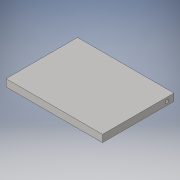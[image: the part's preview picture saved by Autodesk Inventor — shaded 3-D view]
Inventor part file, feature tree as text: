
AUTODESK INVENTOR PART (.ipt)
format: ipt  version: 2016 (Build 200138000, 138)  size: 100,352 bytes
history: native  units: in
note: dims shown in document units (in); Inventor stores cm internally (conversion verified against a paired STEP export)
features: sketch x3, hole x2, extrude x1
ambient origin geometry x8: Origin, YZ Plane, XZ Plane, XY Plane, X Axis, Y Axis, Z Axis, Center Point
bodies: Solid1 (feature_tree)
feature tree (6):
  extrude  "Extrusion1"  Depth=10.0in
  hole  "Hole2"  [1 undecoded]
  hole  "Hole3"  [1 undecoded]
  sketch  "Sketch1"  dims[d0=13.5in d1=10.0in]
  sketch  "Sketch6"  dims[d2=1.0in d3=0.0in d18=1.0in]
  sketch  "Sketch8"  dims[d19=0.5in d20=0.5in d21=0.75in d22=0.375in d23=0.25in d24=0.5635in d25=0.5in d26=0.0in d27=0.5in d28=0.75in d29=0.375in d30=0.25in d31=0.5635in d32=0.5in d33=0.0in]
note: 2 required parameter values undecoded (feature->parameter linkage not recoverable at this tier; creation-order binding heuristic only, values carry confidence <= 0.55)
